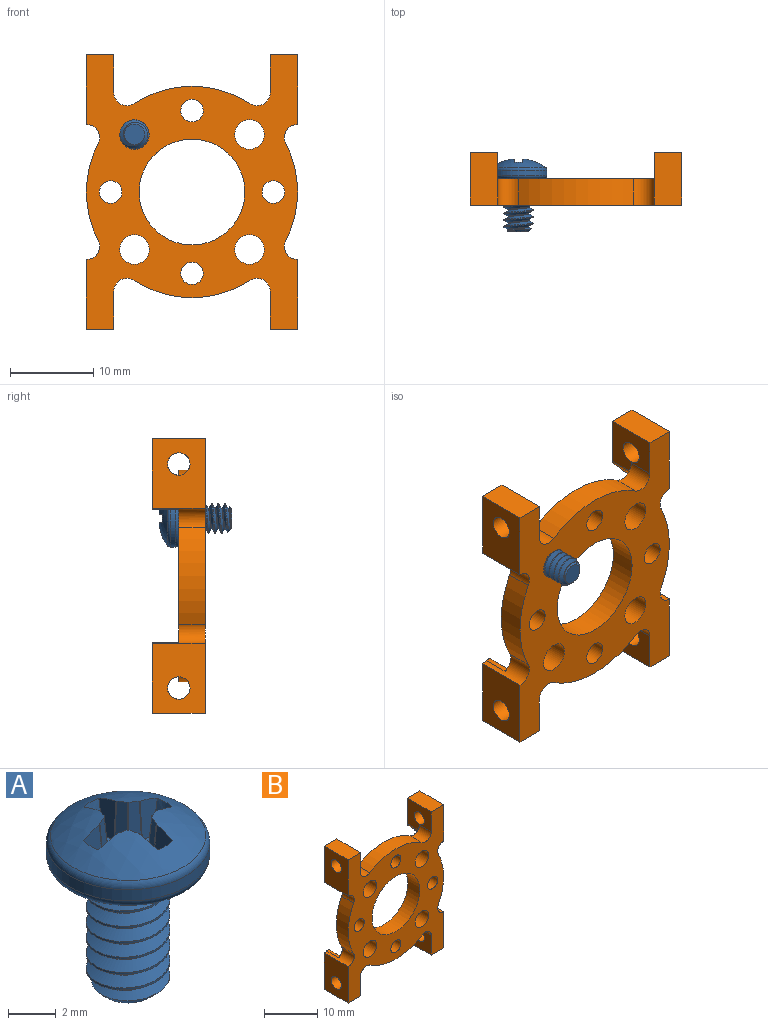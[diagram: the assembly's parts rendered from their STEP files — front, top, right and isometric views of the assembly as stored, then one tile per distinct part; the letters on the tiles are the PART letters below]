
ASSEMBLY  parts=2 mates=1
PART A: 45 faces, bbox 7.7x7.7x9.2 mm
  f0: cone r=2.38mm half-angle=15deg, axis (0,0,1), area 1.3mm2, adj f3,f19,f23,f24
  f1: cone r=2.38mm half-angle=15deg, axis (0,0,1), area 1.3mm2, adj f3,f18,f19,f20
  f2: torus R=2.99mm, axis (0,0,1), area 8.7mm2, adj f3,f4
  f3: sphere r=5.39mm, area 28.4mm2, adj f0,f1,f2,f14,f15,f16,f17,f18
  f4: cylinder r=3.43mm len=6.86mm, axis (0,0,-1), area 12.4mm2, adj f2,f5
  f5: torus R=2.99mm, axis (0,0,1), area 14.3mm2, adj f4,f9
  f6: cone r=4.41mm half-angle=45deg, axis (0,0,1), area 3.3mm2, adj f8,f10,f11,f12,f13
  f7: cylinder r=1.24mm len=6.35mm, axis (0,0,1), area 6.2mm2, adj f9,f10,f11,f12,f13
  f8: cylinder r=1.75mm len=5.83mm, axis (0,0,1), area 8mm2, adj f6,f9,f10,f11
  f9: plane 6.28x6.28mm, normal (0,0,-1), area 20.9mm2, adj f5,f7,f8,f10,f11
  f10: bspline ~6.6x3.5mm, area 42.5mm2, adj f6,f7,f8,f9,f12
  f11: bspline ~6.65x3.5mm, area 42.9mm2, adj f6,f7,f8,f9
  f12: bspline ~2.8x1.46mm, area 0.5mm2, adj f6,f7,f10
  f13: plane 2.47x2.47mm, normal (0,0,-1), area 4.8mm2, adj f6,f7
  f14: cone r=2.38mm half-angle=15deg, axis (0,0,1), area 1.3mm2, adj f3,f15,f19,f32
  f15: plane 1.94x1.03mm, normal (-1,0,0.09), area 1.5mm2, adj f3,f14,f19,f38
  f16: plane 2x0.56mm, normal (-0.92,-0.38,0.09), area 1mm2, adj f3,f19,f37,f38
  f17: plane 2x0.56mm, normal (-0.38,-0.92,0.09), area 1mm2, adj f3,f19,f36,f37
  f18: plane 1.94x1.03mm, normal (0,-1,0.09), area 1.5mm2, adj f1,f3,f19,f36
  f19: plane 3.64x3.64mm, normal (0,0,1), area 5.1mm2, adj f0,f1,f14,f15,f16,f17,f18,f20
  f20: plane 1.94x1.03mm, normal (0,1,0.09), area 1.5mm2, adj f1,f3,f19,f40
  f21: plane 2x0.56mm, normal (-0.38,0.92,0.09), area 1mm2, adj f3,f19,f40,f41
  f22: plane 2x0.56mm, normal (-0.92,0.38,0.09), area 1mm2, adj f3,f19,f39,f41
  f23: plane 1.94x1.03mm, normal (-1,0,0.09), area 1.5mm2, adj f0,f3,f19,f39
  f24: plane 1.94x1.03mm, normal (1,0,0.09), area 1.5mm2, adj f0,f3,f19,f42
  f25: plane 2x0.56mm, normal (0.92,0.38,0.09), area 1mm2, adj f3,f19,f42,f44
  f26: plane 2x0.56mm, normal (0.38,0.92,0.09), area 1mm2, adj f3,f19,f43,f44
  f27: plane 1.94x1.03mm, normal (0,1,0.09), area 1.5mm2, adj f3,f19,f28,f43
  f28: cone r=2.38mm half-angle=15deg, axis (0,0,1), area 1.3mm2, adj f3,f19,f27,f29
  f29: plane 1.94x1.03mm, normal (0,-1,0.09), area 1.5mm2, adj f3,f19,f28,f33
  f30: plane 2x0.56mm, normal (0.38,-0.92,0.09), area 1mm2, adj f3,f19,f33,f34
  f31: plane 2x0.56mm, normal (0.92,-0.38,0.09), area 1mm2, adj f3,f19,f34,f35
  f32: plane 1.94x1.03mm, normal (1,0,0.09), area 1.5mm2, adj f3,f14,f19,f35
  f33: cylinder r=0.1mm len=1.94mm, axis (-0.02,0.09,1), area 0.1mm2, adj f3,f19,f29,f30
  f34: cylinder r=0.1mm len=2mm, axis (-0.07,0.07,1), area 0.2mm2, adj f3,f19,f30,f31
  f35: cylinder r=0.1mm len=1.94mm, axis (-0.09,0.02,1), area 0.1mm2, adj f3,f19,f31,f32
  f36: cylinder r=0.1mm len=1.94mm, axis (0.02,0.09,1), area 0.1mm2, adj f3,f17,f18,f19
  f37: cylinder r=0.1mm len=2mm, axis (0.07,0.07,1), area 0.2mm2, adj f3,f16,f17,f19
  f38: cylinder r=0.1mm len=1.94mm, axis (0.09,0.02,1), area 0.1mm2, adj f3,f15,f16,f19
  f39: cylinder r=0.1mm len=1.94mm, axis (0.09,-0.02,1), area 0.1mm2, adj f3,f19,f22,f23
  f40: cylinder r=0.1mm len=1.94mm, axis (0.02,-0.09,1), area 0.1mm2, adj f3,f19,f20,f21
  f41: cylinder r=0.1mm len=2mm, axis (0.07,-0.07,1), area 0.2mm2, adj f3,f19,f21,f22
  f42: cylinder r=0.1mm len=1.94mm, axis (-0.09,-0.02,1), area 0.1mm2, adj f3,f19,f24,f25
  f43: cylinder r=0.1mm len=1.94mm, axis (-0.02,-0.09,1), area 0.1mm2, adj f3,f19,f26,f27
  f44: cylinder r=0.1mm len=2mm, axis (-0.07,-0.07,1), area 0.2mm2, adj f3,f19,f25,f26
PART B: 55 faces, bbox 25.4x6.4x33 mm
  f0: cylinder r=1.35mm len=3.29mm, axis (-1,0,0), area 28mm2, adj f29,f31
  f1: cylinder r=1.35mm len=3.29mm, axis (-1,0,0), area 28mm2, adj f25,f27
  f2: cylinder r=1.35mm len=3.29mm, axis (1,0,0), area 28mm2, adj f34,f36
  f3: cylinder r=1.35mm len=3.29mm, axis (1,0,0), area 28mm2, adj f37,f39
  f4: cylinder r=0.64mm len=3.18mm, axis (0,-1,0), area 2.7mm2, adj f20,f32,f43,f44
  f5: cylinder r=0.64mm len=3.18mm, axis (0,-1,0), area 2.7mm2, adj f20,f33,f45,f46
  f6: cylinder r=1.59mm len=3.18mm, axis (0,1,0), area 10.8mm2, adj f19,f20,f24,f37
  f7: cylinder r=1.59mm len=3.18mm, axis (0,1,0), area 10.8mm2, adj f20,f22,f24,f36
  f8: cylinder r=1.59mm len=3.18mm, axis (0,1,0), area 10.8mm2, adj f20,f22,f24,f29
  f9: cylinder r=1.59mm len=3.18mm, axis (0,1,0), area 10.8mm2, adj f19,f20,f24,f25
  f10: cylinder r=1.78mm len=3.56mm, axis (0,1,0), area 35.5mm2, adj f20,f24
  f11: cylinder r=1.78mm len=3.56mm, axis (0,1,0), area 35.5mm2, adj f20,f24
  f12: cylinder r=1.78mm len=3.56mm, axis (0,1,0), area 35.5mm2, adj f20,f24
  f13: cylinder r=1.78mm len=3.56mm, axis (0,1,0), area 35.5mm2, adj f20,f24
  f14: cylinder r=1.35mm len=3.18mm, axis (0,1,0), area 27mm2, adj f20,f24
  f15: cylinder r=1.35mm len=3.18mm, axis (0,1,0), area 27mm2, adj f20,f24
  f16: cylinder r=1.35mm len=3.18mm, axis (0,1,0), area 27mm2, adj f20,f24
  f17: cylinder r=1.35mm len=3.18mm, axis (0,1,0), area 27mm2, adj f20,f24
  f18: cylinder r=6.36mm len=12.73mm, axis (0,1,0), area 126.9mm2, adj f20,f24
  f19: cylinder r=12.7mm len=13.9mm, axis (0,-1,0), area 46.7mm2, adj f6,f9,f20,f24
  f20: plane 25.4x25.4mm, normal (0,1,0), area 341.8mm2, adj f4,f5,f6,f7,f8,f9,f10,f11
  f21: cylinder r=12.7mm len=11.64mm, axis (0,-1,0), area 38.4mm2, adj f20,f24,f33,f40
  f22: cylinder r=12.7mm len=13.9mm, axis (0,-1,0), area 46.7mm2, adj f7,f8,f20,f24
  f23: cylinder r=12.7mm len=11.64mm, axis (0,-1,0), area 38.4mm2, adj f20,f24,f28,f32
  f24: plane 33.02x25.4mm, normal (0,-1,0), area 443.4mm2, adj f6,f7,f8,f9,f10,f11,f12,f13
  f25: plane 6.35x5.9mm, normal (1,0,0), area 27.5mm2, adj f1,f9,f20,f24,f26,f42,f51
  f26: plane 6.35x3.29mm, normal (0,0,-1), area 20.9mm2, adj f24,f25,f27,f42
  f27: plane 8.38x6.35mm, normal (-1,0,0), area 47.4mm2, adj f1,f24,f26,f28,f42
  f28: cylinder r=1.59mm len=6.35mm, axis (0,1,0), area 12.4mm2, adj f20,f23,f24,f27,f42,f52
  f29: plane 6.35x5.9mm, normal (1,0,0), area 27.5mm2, adj f0,f8,f20,f24,f30,f44,f50
  f30: plane 6.35x3.29mm, normal (0,0,1), area 20.9mm2, adj f24,f29,f31,f44
  f31: plane 8.38x6.35mm, normal (-1,0,0), area 47.4mm2, adj f0,f24,f30,f32,f44
  f32: cylinder r=1.59mm len=6.35mm, axis (0,1,0), area 12.4mm2, adj f4,f20,f23,f24,f31,f44
  f33: cylinder r=1.59mm len=6.35mm, axis (0,1,0), area 12.4mm2, adj f5,f20,f21,f24,f34,f46
  f34: plane 8.38x6.35mm, normal (1,0,0), area 47.4mm2, adj f2,f24,f33,f35,f46
  f35: plane 6.35x3.29mm, normal (0,0,1), area 20.9mm2, adj f24,f34,f36,f46
  f36: plane 6.35x5.9mm, normal (-1,0,0), area 27.5mm2, adj f2,f7,f20,f24,f35,f46,f49
  f37: plane 6.35x5.9mm, normal (-1,0,0), area 27.5mm2, adj f3,f6,f20,f24,f38,f48,f53
  f38: plane 6.35x3.29mm, normal (0,0,-1), area 20.9mm2, adj f24,f37,f39,f48
  f39: plane 8.38x6.35mm, normal (1,0,0), area 47.4mm2, adj f3,f24,f38,f40,f48
  f40: cylinder r=1.59mm len=6.35mm, axis (0,1,0), area 12.4mm2, adj f20,f21,f24,f39,f48,f54
  f41: cylinder r=13.97mm len=3.18mm, axis (0,-1,0), area 8.2mm2, adj f20,f42,f51,f52
  f42: plane 8.56x3.29mm, normal (0,1,0), area 25.4mm2, adj f25,f26,f27,f28,f41,f51,f52
  f43: cylinder r=13.97mm len=3.18mm, axis (0,-1,0), area 8.2mm2, adj f4,f20,f44,f50
  f44: plane 8.56x3.29mm, normal (0,1,0), area 25.4mm2, adj f4,f29,f30,f31,f32,f43,f50
  f45: cylinder r=13.97mm len=3.18mm, axis (0,-1,0), area 8.2mm2, adj f5,f20,f46,f49
  f46: plane 8.56x3.29mm, normal (0,1,0), area 25.4mm2, adj f5,f33,f34,f35,f36,f45,f49
  f47: cylinder r=13.97mm len=3.18mm, axis (0,-1,0), area 8.2mm2, adj f20,f48,f53,f54
  f48: plane 8.56x3.29mm, normal (0,1,0), area 25.4mm2, adj f37,f38,f39,f40,f47,f53,f54
  f49: cylinder r=0.64mm len=3.18mm, axis (0,-1,0), area 1.6mm2, adj f20,f36,f45,f46
  f50: cylinder r=0.64mm len=3.18mm, axis (0,-1,0), area 1.6mm2, adj f20,f29,f43,f44
  f51: cylinder r=0.64mm len=3.18mm, axis (0,-1,0), area 1.6mm2, adj f20,f25,f41,f42
  f52: cylinder r=0.64mm len=3.18mm, axis (0,-1,0), area 2.7mm2, adj f20,f28,f41,f42
  f53: cylinder r=0.64mm len=3.18mm, axis (0,-1,0), area 1.6mm2, adj f20,f37,f47,f48
  f54: cylinder r=0.64mm len=3.18mm, axis (0,-1,0), area 2.7mm2, adj f20,f40,f47,f48
PLACE A rot(axis=(0,0.71,0.71),180deg) t=(-12.26,8.57,-4.75)mm
PLACE B t=(-5.35,11.75,-11.67)mm
MATE fastened B.f10 <-> A.f5  axis (0,1,0) through (-12.26,14.92,-4.75)mm
